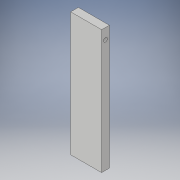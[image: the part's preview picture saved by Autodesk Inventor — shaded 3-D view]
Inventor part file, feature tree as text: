
AUTODESK INVENTOR PART (.ipt)
format: ipt  version: 2017 (Build 210142000, 142)  size: 97,792 bytes
history: native  units: in
note: dims shown in document units (in); Inventor stores cm internally (conversion verified against a paired STEP export)
features: extrude x2, sketch x2
ambient origin geometry x8: Origin, YZ Plane, XZ Plane, XY Plane, X Axis, Y Axis, Z Axis, Center Point
bodies: Solid1 (feature_tree)
feature tree (4):
  extrude  "Extrusion1"  Depth=2.0in
  extrude  "Extrusion2"  Depth=0.5in
  sketch  "Sketch1"  dims[d0=8.0in d1=2.0in]
  sketch  "Sketch2"  dims[d2=0.5in d3=0.0in d4=0.25in d5=5.0in d6=0.0in d7=0.25in]
